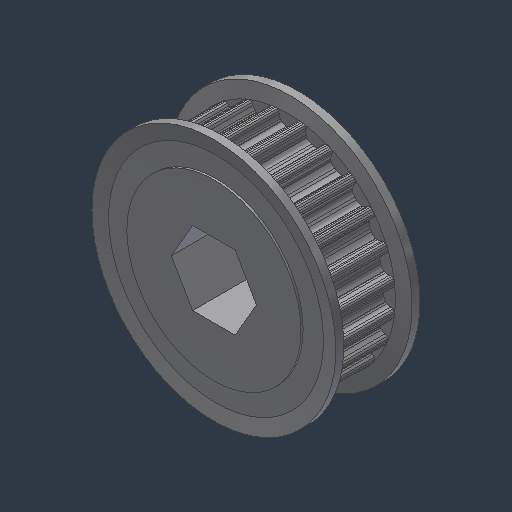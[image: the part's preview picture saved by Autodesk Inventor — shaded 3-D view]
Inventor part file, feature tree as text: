
AUTODESK INVENTOR PART (.ipt)
format: ipt  version: 2024.3 (Build 283343000, 343)  size: 605,696 bytes
history: native  units: mm (DEFAULTED — no unit token found)
features: mirror x1
ambient origin geometry x8: Origin, YZ Plane, XZ Plane, XY Plane, X Axis, Y Axis, Z Axis, Center Point
bodies: Solid1 (feature_tree)
feature tree (1):
  mirror  "Mirror1"
